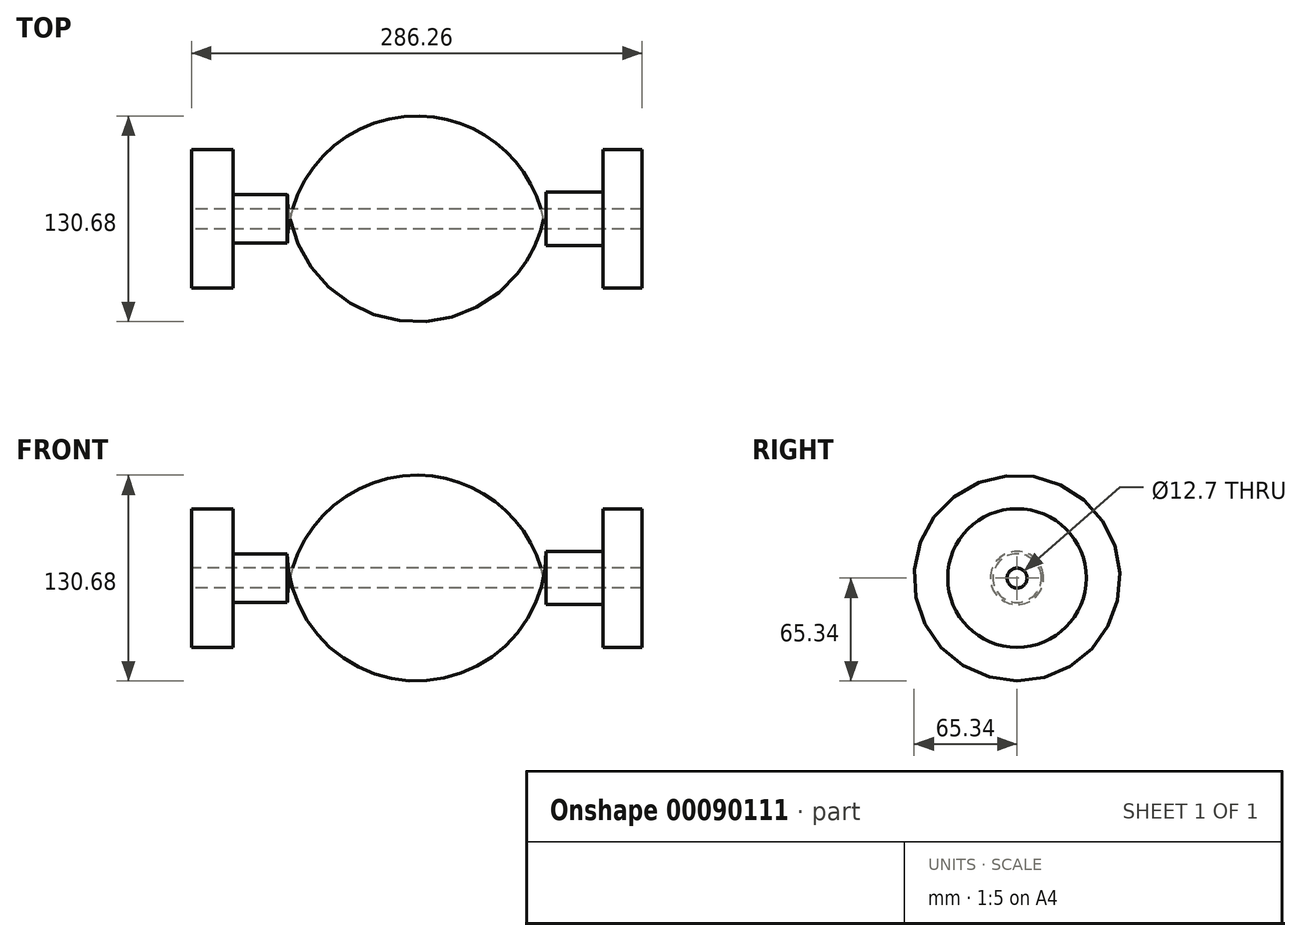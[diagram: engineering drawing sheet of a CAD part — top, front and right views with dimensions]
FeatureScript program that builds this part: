
annotation { "Feature Type Name" : "Feature", "Feature Type Description" : "" }
export const myFeature = defineFeature(function(context is Context, id is Id, definition is map)
    precondition{}
    {
        {
            var Q0;
            Q0=qCreatedBy(makeId("Front.planeOp"),FACE);
            var sketch = newSketch(context, id + "F0", { "sketchPlane" : qUnion([Q0])});
            skLineSegment(sketch, "E0", {"start": v(143.13, 6.35) * mm, "end": v(143.13, 44.04) * mm});
            skLineSegment(sketch, "E1", {"start": v(143.13, 44.04) * mm, "end": v(118.17, 44.04) * mm});
            skLineSegment(sketch, "E2", {"start": v(118.17, 44.04) * mm, "end": v(118.17, 16.88) * mm});
            skLineSegment(sketch, "E3", {"start": v(118.17, 16.88) * mm, "end": v(82.22, 16.88) * mm});
            skArc(sketch, "E4", {"start": v(82.22, 16.88) * mm, "mid": v(-0.73, 99.1) * mm, "end": v(-82.2, 15.41) * mm});
            skLineSegment(sketch, "E5", {"start": v(-143.13, 6.35) * mm, "end": v(-143.13, 44.04) * mm});
            skLineSegment(sketch, "E6", {"start": v(-143.13, 44.04) * mm, "end": v(-116.7, 44.04) * mm});
            skLineSegment(sketch, "E7", {"start": v(-116.7, 44.04) * mm, "end": v(-116.7, 15.41) * mm});
            skLineSegment(sketch, "E8", {"start": v(-116.7, 15.41) * mm, "end": v(-82.2, 15.41) * mm});
            skLineSegment(sketch, "E9", {"start": v(-82.2, 15.41) * mm, "end": v(-116.7, 15.41) * mm});
            skPoint(sketch, "E10.orphan", {"position": v(78.54, 16.88) * mm});
            skLineSegment(sketch, "E11", {"start": v(-143.13, 6.35) * mm, "end": v(143.13, 6.35) * mm});
            skPoint(sketch, "E12.start.orphan", {"position": v(-107.9, 0) * mm});
            skLineSegment(sketch, "E13", {"start": v(-153.1, 0) * mm, "end": v(154.36, 0) * mm, "construction": true});
            skSolve(sketch);
        }
        {
            var Q0;
            Q0=makeQuery(id+"F0.imprint","IMPRINT",FACE,{"disambiguationData":[TD([[makeQuery(id+"F0.imprint","IMPRINT",EDGE,{"derivedFrom":sQuery(id+"F0.wireOp",EDGE,"E0")}),1.0]])]});
            var Q1;
            Q1=sQuery(id+"F0.wireOp",EDGE,"E13");
            revolve(context, id + "F1", {"entities" : qUnion([Q0]), "axis" : qUnion([Q1]), "revolveType" : RevolveType.FULL});
        }
    });
